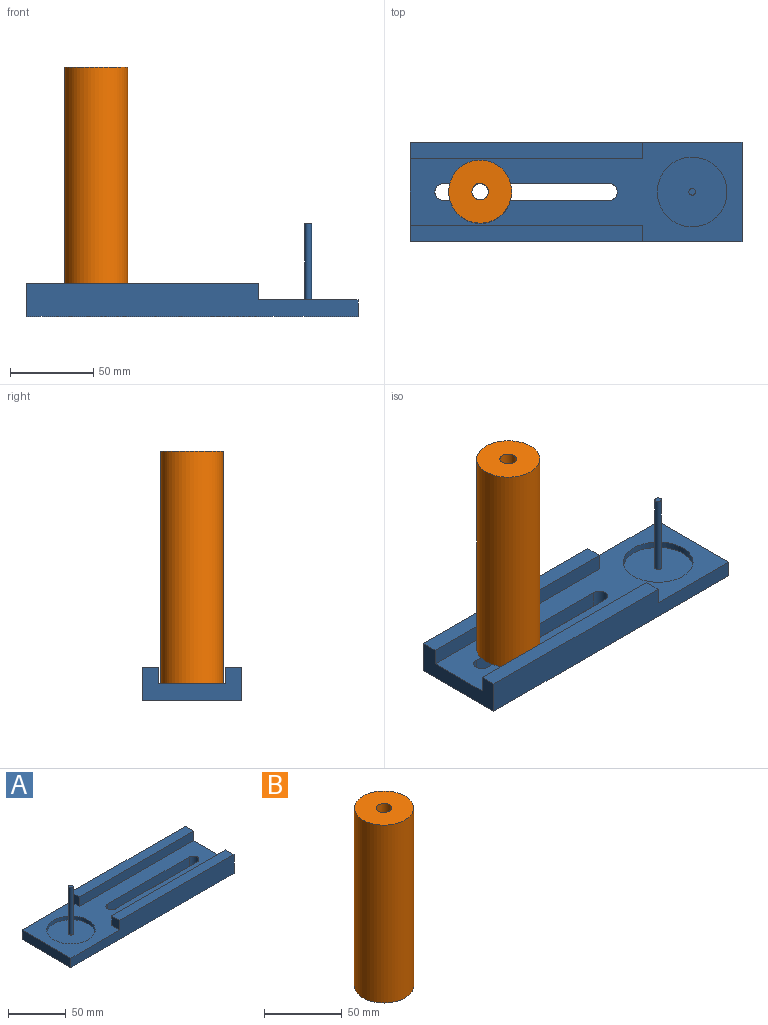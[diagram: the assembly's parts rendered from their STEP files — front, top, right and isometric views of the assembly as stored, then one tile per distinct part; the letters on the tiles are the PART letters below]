
ASSEMBLY  parts=2 mates=2
PART A: 20 faces, bbox 200x60x56 mm
  f0: plane 200x20mm, normal (0,-1,0), area 3400mm2, adj f1,f8,f9,f10,f14,f16
  f1: plane 60x20mm, normal (1,0,0), area 800mm2, adj f0,f2,f9,f10,f12,f13,f15,f16
  f2: plane 200x20mm, normal (0,1,0), area 3400mm2, adj f1,f8,f9,f10,f11,f13
  f3: plane 100x10mm, normal (0,1,0), area 1000mm2, adj f4,f7,f9,f10
  f4: cylinder r=5mm len=10mm, axis (0,0,-1), area 157.1mm2, adj f3,f5,f9,f10
  f5: plane 100x10mm, normal (0,-1,0), area 1000mm2, adj f4,f7,f9,f10
  f6: cylinder r=21mm len=42mm, axis (0,0,-1), area 527.8mm2, adj f9,f17
  f7: cylinder r=5mm len=10mm, axis (0,0,-1), area 157.1mm2, adj f3,f5,f9,f10
  f8: plane 60x10mm, normal (-1,0,0), area 600mm2, adj f0,f2,f9,f10
  f9: plane 200x60mm, normal (0,0,1), area 6736mm2, adj f0,f1,f2,f3,f4,f5,f6,f7
  f10: plane 200x60mm, normal (0,0,-1), area 10921.5mm2, adj f0,f1,f2,f3,f4,f5,f7,f8
  f11: plane 10x10mm, normal (-1,0,0), area 100mm2, adj f2,f9,f12,f13
  f12: plane 140x10mm, normal (0,-1,0), area 1400mm2, adj f1,f9,f11,f13
  f13: plane 140x10mm, normal (0,0,1), area 1400mm2, adj f1,f2,f11,f12
  f14: plane 10x10mm, normal (-1,0,0), area 100mm2, adj f0,f9,f15,f16
  f15: plane 140x10mm, normal (0,1,0), area 1400mm2, adj f1,f9,f14,f16
  f16: plane 140x10mm, normal (0,0,1), area 1400mm2, adj f0,f1,f14,f15
  f17: plane 42x42mm, normal (0,0,1), area 1372.9mm2, adj f6,f18
  f18: cylinder r=2mm len=50mm, axis (0,0,-1), area 628.3mm2, adj f17,f19
  f19: plane 4x4mm, normal (0,0,1), area 12.6mm2, adj f18
PART B: 4 faces, bbox 38x38x140 mm
  f0: cylinder r=5mm len=140mm, axis (0,0,-1), area 4398.2mm2, adj f2,f3
  f1: cylinder r=19mm len=140mm, axis (0,0,-1), area 16713.3mm2, adj f2,f3
  f2: plane 38x38mm, normal (0,0,1), area 1055.6mm2, adj f0,f1
  f3: plane 38x38mm, normal (0,0,-1), area 1055.6mm2, adj f0,f1
PLACE A rot(axis=(0,0,1),180deg) t=(-59.32,-183.92,65.34)mm
PLACE B rot(axis=(0,0,1),0deg) t=(-94.05,-183.92,75.34)mm
MATE pin_slot B.f1 <-> A.f4  axis (0,0,-1) through (-94.05,-183.92,75.34)mm
MATE parallel B.f1 <-> A.f9  axis (0,0,-1) through (-94.05,-183.92,75.34)mm
